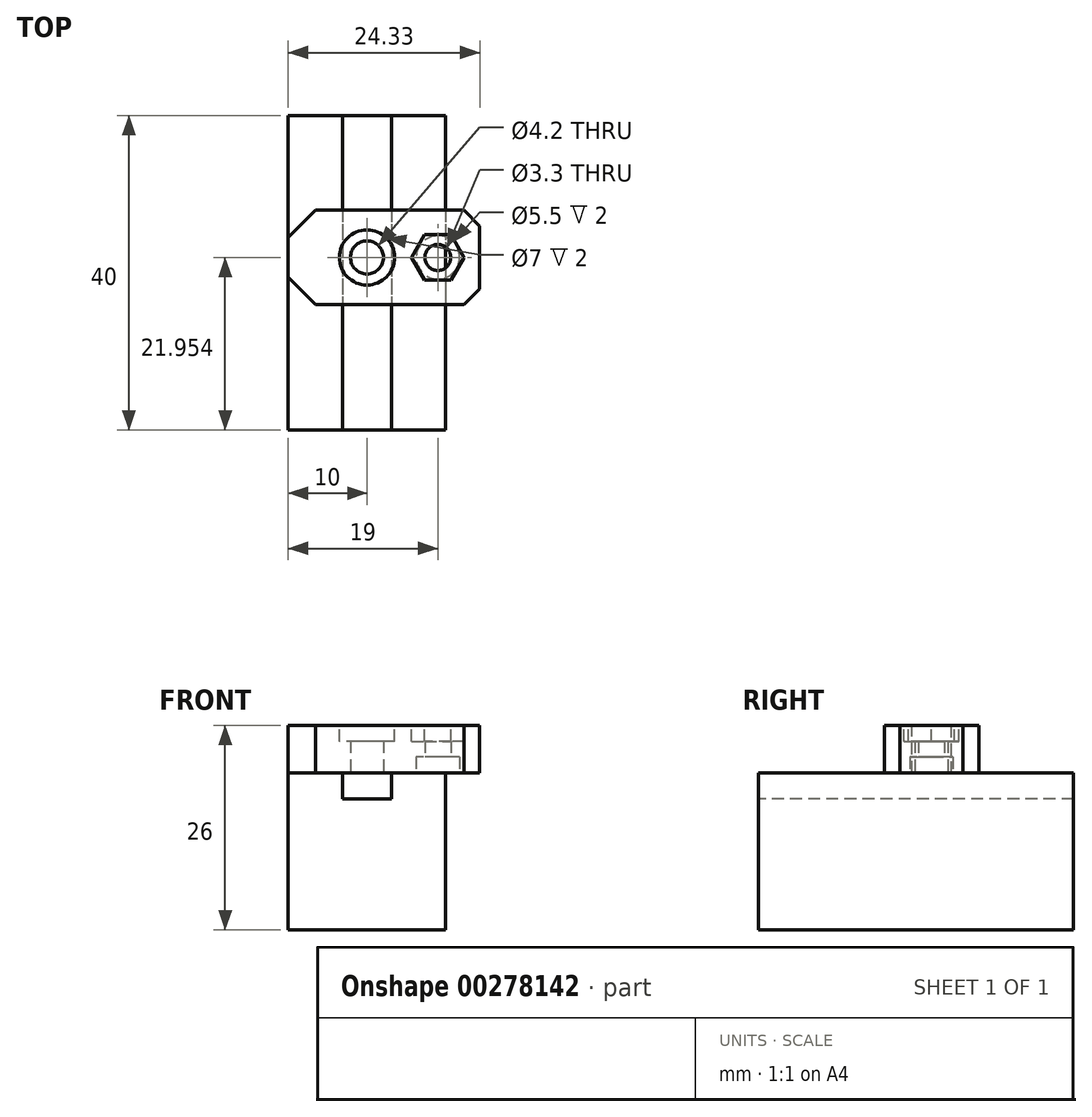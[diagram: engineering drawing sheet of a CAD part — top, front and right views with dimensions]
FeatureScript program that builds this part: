
annotation { "Feature Type Name" : "Feature", "Feature Type Description" : "" }
export const myFeature = defineFeature(function(context is Context, id is Id, definition is map)
    precondition{}
    {
        {
            var Q0;
            Q0=qCreatedBy(makeId("Front.planeOp"),FACE);
            var sketch = newSketch(context, id + "F0", { "sketchPlane" : qUnion([Q0])});
            skLineSegment(sketch, "E0.bottom", {"start": v(0, 0) * mm, "end": v(20, 0) * mm});
            skLineSegment(sketch, "E0.top", {"start": v(0, 20) * mm, "end": v(20, 20) * mm});
            skLineSegment(sketch, "E0.left", {"start": v(0, 0) * mm, "end": v(0, 20) * mm});
            skLineSegment(sketch, "E0.right", {"start": v(20, 0) * mm, "end": v(20, 20) * mm});
            skLineSegment(sketch, "E1.bottom", {"start": v(6.9, 20) * mm, "end": v(13.1, 20) * mm});
            skLineSegment(sketch, "E1.top", {"start": v(6.9, 16.64) * mm, "end": v(13.1, 16.64) * mm});
            skLineSegment(sketch, "E1.left", {"start": v(6.9, 20) * mm, "end": v(6.9, 16.64) * mm});
            skLineSegment(sketch, "E1.right", {"start": v(13.1, 20) * mm, "end": v(13.1, 16.64) * mm});
            skSolve(sketch);
        }
        {
            var Q0;
            Q0=makeQuery(id+"F0.imprint","IMPRINT",FACE,{"disambiguationData":[TD([[makeQuery(id+"F0.imprint","IMPRINT",EDGE,{"derivedFrom":sQuery(id+"F0.wireOp",EDGE,"E0.bottom")}),1.0]])]});
            extrude(context, id + "F1", {"entities" : qUnion([Q0]), "oppositeDirection" : true, "depth" : 40 * mm});
        }
        {
            var Q0;
            {var subQ0=sQuery(id+"F0.wireOp",EDGE,"E0.top");Q0=makeQuery(id+"F1.opExtrude","SWEPT_FACE",FACE,{"disambiguationData":[OSD([subQ0]),TDD([makeQuery(id+"F0.imprint","IMPRINT",EDGE,{"disambiguationData":[TD([[makeQuery(id+"F0.imprint","INTERSECT",VERTEX,{"derivedFrom":[subQ0,sQuery(id+"F0.wireOp",EDGE,"E0.left")]}),-1.0]])],"derivedFrom":subQ0})])]});}
            var sketch = newSketch(context, id + "F2", { "sketchPlane" : qUnion([Q0])});
            skLineSegment(sketch, "E2.bottom", {"start": v(0, 27.95) * mm, "end": v(20, 27.95) * mm});
            skLineSegment(sketch, "E2.top", {"start": v(0, 15.95) * mm, "end": v(20, 15.95) * mm});
            skLineSegment(sketch, "E2.left", {"start": v(0, 27.95) * mm, "end": v(0, 15.95) * mm});
            skLineSegment(sketch, "E2.right", {"start": v(20, 27.95) * mm, "end": v(20, 15.95) * mm});
            skCircle(sketch, "E3", {"center": v(10, 21.95) * mm, "radius": 2.1 * mm});
            skCircle(sketch, "E4", {"center": v(19, 21.95) * mm, "radius": 2.75 * mm});
            skCircle(sketch, "E5", {"center": v(19, 21.95) * mm, "radius": 1.65 * mm});
            skLineSegment(sketch, "E6.bottom", {"start": v(20, 27.95) * mm, "end": v(24.33, 27.95) * mm});
            skLineSegment(sketch, "E6.top", {"start": v(20, 15.95) * mm, "end": v(24.33, 15.95) * mm});
            skLineSegment(sketch, "E6.right", {"start": v(24.33, 27.95) * mm, "end": v(24.33, 15.95) * mm});
            skSolve(sketch);
        }
        {
            var Q0;
            {var subQ0=sQuery(id+"F2.wireOp",EDGE,"E2.left");Q0=makeQuery(id+"F2.imprint","IMPRINT",FACE,{"disambiguationData":[TD([[makeQuery(id+"F2.imprint","IMPRINT",EDGE,{"derivedFrom":subQ0}),1.0]])]});}
            var Q1;
            Q1=makeQuery(id+"F2.imprint","IMPRINT",FACE,{"disambiguationData":[TD([[makeQuery(id+"F2.imprint","IMPRINT",EDGE,{"derivedFrom":sQuery(id+"F2.wireOp",EDGE,"E3")}),-1.0]])]});
            var Q2;
            {var subQ0=sQuery(id+"F2.wireOp",EDGE,"E2.right");var subQ1=sQuery(id+"F2.wireOp",EDGE,"E4");var subQ2=makeQuery(id+"F2.imprint","INTERSECT",VERTEX,{"disambiguationData":[OD(0.0)],"derivedFrom":[subQ1,subQ0]});Q2=makeQuery(id+"F2.imprint","IMPRINT",FACE,{"disambiguationData":[TD([[makeQuery(id+"F2.imprint","IMPRINT",EDGE,{"disambiguationData":[TD([[subQ2,1.0]])],"derivedFrom":subQ1}),1.0]])]});}
            var Q3;
            {var subQ0=sQuery(id+"F2.wireOp",EDGE,"E2.right");var subQ1=sQuery(id+"F2.wireOp",EDGE,"E4");var subQ2=makeQuery(id+"F2.imprint","INTERSECT",VERTEX,{"disambiguationData":[OD(0.0)],"derivedFrom":[subQ1,subQ0]});Q3=makeQuery(id+"F2.imprint","IMPRINT",FACE,{"disambiguationData":[TD([[makeQuery(id+"F2.imprint","IMPRINT",EDGE,{"disambiguationData":[TD([[subQ2,-1.0]])],"derivedFrom":subQ1}),1.0]])]});}
            var Q4;
            {var subQ1=sQuery(id+"F2.wireOp",EDGE,"E6.bottom");Q4=makeQuery(id+"F2.imprint","IMPRINT",FACE,{"disambiguationData":[TD([[makeQuery(id+"F2.imprint","IMPRINT",EDGE,{"derivedFrom":subQ1}),-1.0]])]});}
            extrude(context, id + "F3", {"entities" : qUnion([Q0, Q1, Q2, Q3, Q4]), "depth" : 6 * mm});
        }
        {
            var Q0;
            Q0=makeQuery(id+"F3.opExtrude","SWEPT_EDGE",EDGE,{"disambiguationData":[OSD([sQuery(id+"F0.wireOp",EDGE,"E0.top"),sQuery(id+"F0.wireOp",EDGE,"E0.left"),sQuery(id+"F2.wireOp",EDGE,"E2.bottom"),sQuery(id+"F2.wireOp",EDGE,"E2.left")])]});
            var Q1;
            Q1=makeQuery(id+"F3.opExtrude","SWEPT_EDGE",EDGE,{"disambiguationData":[OSD([sQuery(id+"F0.wireOp",EDGE,"E0.top"),sQuery(id+"F0.wireOp",EDGE,"E0.left"),sQuery(id+"F2.wireOp",EDGE,"E2.top"),sQuery(id+"F2.wireOp",EDGE,"E2.left")])]});
            chamfer(context, id + "F4", {"entities" : qUnion([Q0, Q1]), "width" : 3.5 * mm, "tangentPropagation" : true});
        }
        {
            var Q0;
            Q0=makeQuery(id+"F3.opExtrude","SWEPT_EDGE",EDGE,{"disambiguationData":[OSD([sQuery(id+"F2.wireOp",EDGE,"E6.top"),sQuery(id+"F2.wireOp",EDGE,"E6.right")])]});
            var Q1;
            Q1=makeQuery(id+"F3.opExtrude","SWEPT_EDGE",EDGE,{"disambiguationData":[OSD([sQuery(id+"F2.wireOp",EDGE,"E6.bottom"),sQuery(id+"F2.wireOp",EDGE,"E6.right")])]});
            chamfer(context, id + "F5", {"entities" : qUnion([Q0, Q1]), "width" : 2 * mm, "tangentPropagation" : true});
        }
        {
            var Q0;
            {var subQ0=sQuery(id+"F2.wireOp",EDGE,"E2.right");var subQ1=sQuery(id+"F2.wireOp",EDGE,"E4");var subQ2=makeQuery(id+"F2.imprint","INTERSECT",VERTEX,{"disambiguationData":[OD(0.0)],"derivedFrom":[subQ1,subQ0]});Q0=makeQuery(id+"F2.imprint","IMPRINT",FACE,{"disambiguationData":[TD([[makeQuery(id+"F2.imprint","IMPRINT",EDGE,{"disambiguationData":[TD([[subQ2,1.0]])],"derivedFrom":subQ1}),1.0]])]});}
            var Q1;
            {var subQ0=sQuery(id+"F2.wireOp",EDGE,"E2.right");var subQ1=sQuery(id+"F2.wireOp",EDGE,"E4");var subQ2=makeQuery(id+"F2.imprint","INTERSECT",VERTEX,{"disambiguationData":[OD(0.0)],"derivedFrom":[subQ1,subQ0]});Q1=makeQuery(id+"F2.imprint","IMPRINT",FACE,{"disambiguationData":[TD([[makeQuery(id+"F2.imprint","IMPRINT",EDGE,{"disambiguationData":[TD([[subQ2,-1.0]])],"derivedFrom":subQ1}),1.0]])]});}
            extrude(context, id + "F6", {"entities" : qUnion([Q0, Q1]), "operationType" : NewBodyOperationType.REMOVE, "depth" : 2 * mm});
        }
        {
            var Q0;
            Q0=makeQuery(id+"F3.opExtrude","CAP_FACE",FACE,{"disambiguationData":[OSD([sQuery(id+"F2.wireOp",EDGE,"E2.bottom"),sQuery(id+"F2.wireOp",EDGE,"E2.top"),sQuery(id+"F2.wireOp",EDGE,"E2.left"),sQuery(id+"F2.wireOp",EDGE,"E3"),sQuery(id+"F2.wireOp",EDGE,"E5"),sQuery(id+"F2.wireOp",EDGE,"E6.bottom"),sQuery(id+"F2.wireOp",EDGE,"E6.top"),sQuery(id+"F2.wireOp",EDGE,"E6.right")])],"isStart":false});
            var sketch = newSketch(context, id + "F7", { "sketchPlane" : qUnion([Q0])});
            skCircle(sketch, "E7.cCircle", {"center": v(19, 21.95) * mm, "radius": 2.9 * mm, "construction": true});
            skLineSegment(sketch, "E7.0", {"start": v(17.33, 24.85) * mm, "end": v(20.67, 24.85) * mm});
            skLineSegment(sketch, "E7.1", {"start": v(20.67, 24.85) * mm, "end": v(22.35, 21.95) * mm});
            skLineSegment(sketch, "E7.2", {"start": v(22.35, 21.95) * mm, "end": v(20.67, 19.05) * mm});
            skLineSegment(sketch, "E7.3", {"start": v(20.67, 19.05) * mm, "end": v(17.33, 19.05) * mm});
            skLineSegment(sketch, "E7.4", {"start": v(17.33, 19.05) * mm, "end": v(15.65, 21.95) * mm});
            skLineSegment(sketch, "E7.5", {"start": v(15.65, 21.95) * mm, "end": v(17.33, 24.85) * mm});
            skPoint(sketch, "E7.0.midPoint", {"position": v(19, 24.85) * mm});
            skCircle(sketch, "E8", {"center": v(10, 21.95) * mm, "radius": 3.5 * mm});
            skSolve(sketch);
        }
        {
            var Q0;
            Q0=makeQuery(id+"F7.imprint","IMPRINT",FACE,{"disambiguationData":[TD([[makeQuery(id+"F7.imprint","IMPRINT",EDGE,{"derivedFrom":sQuery(id+"F7.wireOp",EDGE,"E7.0")}),-1.0]])]});
            var Q1;
            Q1=makeQuery(id+"F7.imprint","IMPRINT",FACE,{"disambiguationData":[TD([[makeQuery(id+"F7.imprint","IMPRINT",EDGE,{"derivedFrom":sQuery(id+"F7.wireOp",EDGE,"E8")}),1.0]])]});
            extrude(context, id + "F8", {"entities" : qUnion([Q0, Q1]), "operationType" : NewBodyOperationType.REMOVE, "oppositeDirection" : true, "depth" : 2 * mm});
        }
    });
